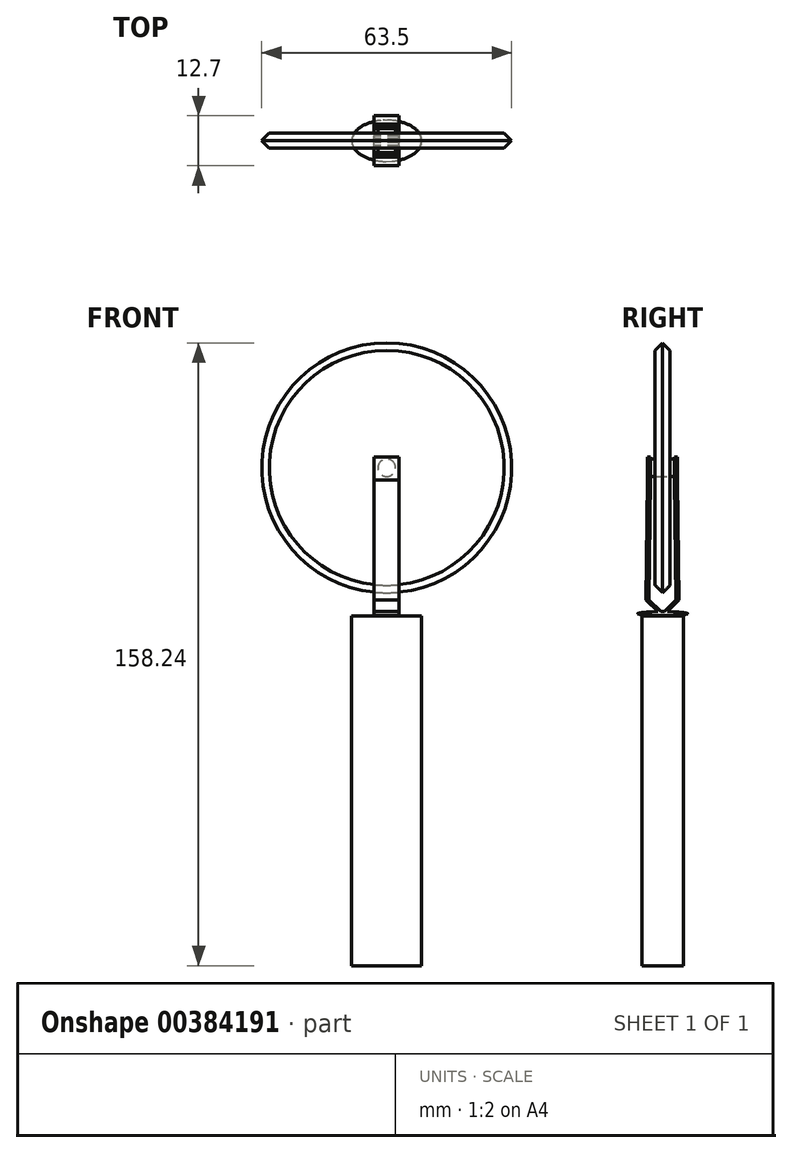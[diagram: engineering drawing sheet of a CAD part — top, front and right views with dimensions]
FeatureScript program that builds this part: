
annotation { "Feature Type Name" : "Feature", "Feature Type Description" : "" }
export const myFeature = defineFeature(function(context is Context, id is Id, definition is map)
    precondition{}
    {
        {
            var Q0;
            Q0=qCreatedBy(makeId("Front.planeOp"),FACE);
            var sketch = newSketch(context, id + "F0", { "sketchPlane" : qUnion([Q0])});
            skCircle(sketch, "E0", {"center": v(0, 0) * mm, "radius": 31.75 * mm});
            skSolve(sketch);
        }
        {
            var Q0;
            Q0=makeQuery(id+"F0.imprint","IMPRINT",FACE,{"disambiguationData":[TD([[makeQuery(id+"F0.imprint","IMPRINT",EDGE,{"derivedFrom":sQuery(id+"F0.wireOp",EDGE,"E0")}),1.0]])]});
            extrude(context, id + "F1", {"entities" : qUnion([Q0]), "endBound" : BoundingType.SYMMETRIC, "depth" : 3.8 * mm});
        }
        {
            var Q0;
            Q0=makeQuery(id+"F1.opExtrude","SWEPT_FACE",FACE,{"disambiguationData":[OSD([sQuery(id+"F0.wireOp",EDGE,"E0")])]});
            chamfer(context, id + "F2", {"entities" : qUnion([Q0]), "width" : 1.9 * mm, "tangentPropagation" : true});
        }
        {
            var Q0;
            Q0=qCreatedBy(makeId("Right.planeOp"),FACE);
            var sketch = newSketch(context, id + "F3", { "sketchPlane" : qUnion([Q0])});
            skLineSegment(sketch, "E1", {"start": v(-3.05, 0) * mm, "end": v(-3.05, 2.8) * mm});
            skLineSegment(sketch, "E2", {"start": v(-3.05, 2.8) * mm, "end": v(-3.81, 2.8) * mm});
            skLineSegment(sketch, "E3", {"start": v(-3.81, 2.8) * mm, "end": v(-3.81, -3.07) * mm});
            skLineSegment(sketch, "E4", {"start": v(-3.81, -3.07) * mm, "end": v(-3.05, -3.07) * mm});
            skLineSegment(sketch, "E5", {"start": v(-3.05, -3.07) * mm, "end": v(-3.05, 0) * mm});
            skLineSegment(sketch, "E6", {"start": v(-3.81, -3.07) * mm, "end": v(-4.2, -33.55) * mm});
            skLineSegment(sketch, "E7", {"start": v(-3.05, -3.07) * mm, "end": v(-3.43, -33.55) * mm});
            skPoint(sketch, "E7.endSnap0", {"position": v(-3.43, -3.07) * mm});
            skLineSegment(sketch, "E8", {"start": v(-3.43, -33.55) * mm, "end": v(0, -37.03) * mm});
            skLineSegment(sketch, "E9", {"start": v(-4.2, -33.55) * mm, "end": v(-0.74, -37.03) * mm});
            skLineSegment(sketch, "E10.MirrorCS", {"start": v(3.81, -3.07) * mm, "end": v(3.05, -3.07) * mm});
            skLineSegment(sketch, "E11.MirrorCS", {"start": v(3.81, 2.8) * mm, "end": v(3.81, -3.07) * mm});
            skLineSegment(sketch, "E12.MirrorCS", {"start": v(3.05, -3.07) * mm, "end": v(3.05, 0) * mm});
            skLineSegment(sketch, "E13.MirrorCS", {"start": v(3.05, 0) * mm, "end": v(3.05, 2.8) * mm});
            skLineSegment(sketch, "E14.MirrorCS", {"start": v(3.05, 2.8) * mm, "end": v(3.81, 2.8) * mm});
            skLineSegment(sketch, "E15.MirrorCS", {"start": v(4.2, -33.55) * mm, "end": v(0.74, -37.03) * mm});
            skLineSegment(sketch, "E16.MirrorCS", {"start": v(3.43, -33.55) * mm, "end": v(0, -37.03) * mm});
            skLineSegment(sketch, "E17.MirrorCS", {"start": v(3.81, -3.07) * mm, "end": v(4.2, -33.55) * mm});
            skLineSegment(sketch, "E18.MirrorCS", {"start": v(3.05, -3.07) * mm, "end": v(3.43, -33.55) * mm});
            skPoint(sketch, "E19.MirrorP", {"position": v(3.43, -3.07) * mm});
            skEllipse(sketch, "E20", {"center": v(0, -37.03) * mm, "majorRadius": 6.35 * mm, "minorRadius": 0.5 * mm, "majorAxis": v(-1, 0)});
            skSolve(sketch);
        }
        {
            var Q0;
            Q0=makeQuery(id+"F3.imprint","IMPRINT",FACE,{"disambiguationData":[TD([[makeQuery(id+"F3.imprint","IMPRINT",EDGE,{"derivedFrom":sQuery(id+"F3.wireOp",EDGE,"E4")}),-1.0]])]});
            var Q1;
            {var subQ3=sQuery(id+"F3.wireOp",EDGE,"xahiSEmn-KcF1-zksE-gHJ4-Nvulb8Trj7Qy");Q1=makeQuery(id+"F3.imprint","IMPRINT",FACE,{"disambiguationData":[TD([[makeQuery(id+"F3.imprint","IMPRINT",EDGE,{"derivedFrom":subQ3}),-1.0]])]});}
            var Q2;
            Q2=makeQuery(id+"F3.imprint","IMPRINT",FACE,{"disambiguationData":[TD([[makeQuery(id+"F3.imprint","IMPRINT",EDGE,{"derivedFrom":sQuery(id+"F3.wireOp",EDGE,"E10.MirrorCS")}),1.0]])]});
            var Q3;
            {var subQ2=sQuery(id+"F3.wireOp",EDGE,"xahiSEmn-KcF1-zksE-gHJ4-Nvulb8Trj7Qy");Q3=makeQuery(id+"F3.imprint","IMPRINT",FACE,{"disambiguationData":[TD([[makeQuery(id+"F3.imprint","IMPRINT",EDGE,{"derivedFrom":subQ2}),1.0]])]});}
            var Q4;
            {var subQ0=sQuery(id+"F3.wireOp",EDGE,"E2");Q4=makeQuery(id+"F3.imprint","IMPRINT",FACE,{"disambiguationData":[TD([[makeQuery(id+"F3.imprint","IMPRINT",EDGE,{"derivedFrom":subQ0}),1.0]])]});}
            var Q5;
            {var subQ2=sQuery(id+"F3.wireOp",EDGE,"E16.MirrorCS");var subQ5=sQuery(id+"F3.wireOp",EDGE,"E8");var subQ7=makeQuery(id+"F3.imprint","INTERSECT",VERTEX,{"derivedFrom":[subQ5,subQ2]});Q5=makeQuery(id+"F3.imprint","IMPRINT",FACE,{"disambiguationData":[TD([[makeQuery(id+"F3.imprint","IMPRINT",EDGE,{"disambiguationData":[TD([[subQ7,1.0]])],"derivedFrom":subQ5}),-1.0]])]});}
            var Q6;
            {var subQ1=sQuery(id+"F3.wireOp",EDGE,"E10.MirrorCS");Q6=makeQuery(id+"F3.imprint","IMPRINT",FACE,{"disambiguationData":[TD([[makeQuery(id+"F3.imprint","IMPRINT",EDGE,{"derivedFrom":subQ1}),-1.0]])]});}
            var Q7;
            {var subQ0=sQuery(id+"F3.wireOp",EDGE,"E16.MirrorCS");var subQ1=sQuery(id+"F3.wireOp",EDGE,"E8");var subQ2=makeQuery(id+"F3.imprint","INTERSECT",VERTEX,{"derivedFrom":[subQ1,subQ0]});Q7=makeQuery(id+"F3.imprint","IMPRINT",FACE,{"disambiguationData":[TD([[makeQuery(id+"F3.imprint","IMPRINT",EDGE,{"disambiguationData":[TD([[subQ2,1.0]])],"derivedFrom":subQ1}),1.0]])]});}
            extrude(context, id + "F4", {"entities" : qUnion([Q0, Q1, Q2, Q3, Q4, Q5, Q6, Q7]), "operationType" : NewBodyOperationType.ADD, "endBound" : BoundingType.SYMMETRIC, "depth" : 6.35 * mm});
        }
        {
            var Q0;
            Q0=qCreatedBy(makeId("Front.planeOp"),FACE);
            var sketch = newSketch(context, id + "F5", { "sketchPlane" : qUnion([Q0])});
            skCircle(sketch, "E21", {"center": v(0, 0) * mm, "radius": 2.23 * mm});
            skSolve(sketch);
        }
        {
            var Q0;
            Q0 = qSketchRegion(id + "F5", true);
            extrude(context, id + "F6", {"entities" : qUnion([Q0]), "endBound" : BoundingType.SYMMETRIC, "depth" : 7.57 * mm});
        }
        {
            var Q0;
            Q0=qCreatedBy(makeId("Top.planeOp"),FACE);
            cPlane(context, id + "F7", {"entities" : qUnion([Q0]), "cplaneType" : CPlaneType.OFFSET, "offset" : 37.6 * mm, "oppositeDirection" : true, "width" : 152.4 * mm, "height" : 152.4 * mm});
        }
        {
            var Q0;
            Q0=qCreatedBy(id+"F7.planeOp",FACE);
            var sketch = newSketch(context, id + "F8", { "sketchPlane" : qUnion([Q0])});
            skEllipse(sketch, "E22", {"center": v(0, 0) * mm, "majorRadius": 8.9 * mm, "minorRadius": 5.26 * mm, "majorAxis": v(1, 0)});
            skSolve(sketch);
        }
        {
            var Q0;
            Q0 = qSketchRegion(id + "F8", true);
            extrude(context, id + "F9", {"entities" : qUnion([Q0]), "oppositeDirection" : true, "depth" : 88.9 * mm});
        }
    });
